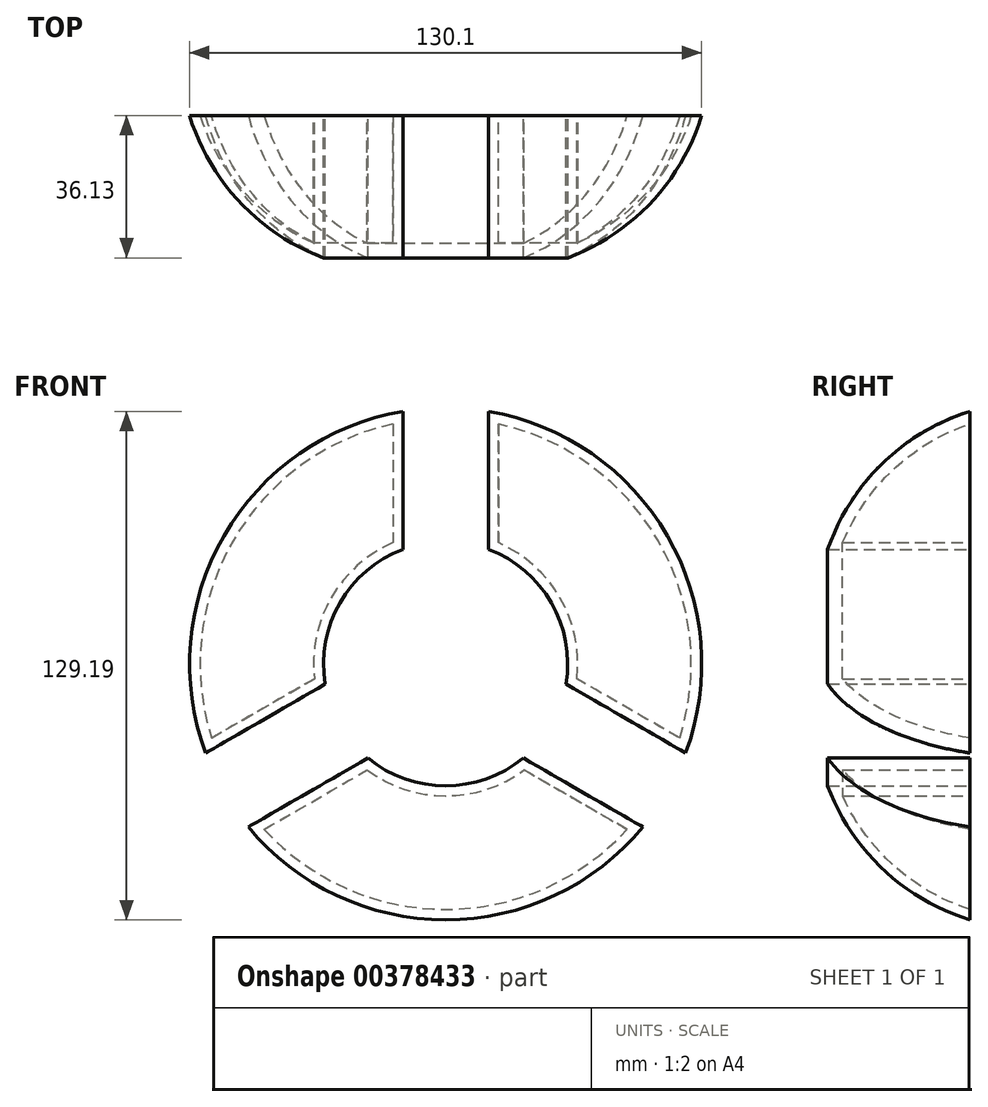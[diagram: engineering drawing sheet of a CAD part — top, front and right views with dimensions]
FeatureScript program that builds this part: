
annotation { "Feature Type Name" : "Feature", "Feature Type Description" : "" }
export const myFeature = defineFeature(function(context is Context, id is Id, definition is map)
    precondition{}
    {
        {
            var Q0;
            Q0=qCreatedBy(makeId("Front.planeOp"),FACE);
            var sketch = newSketch(context, id + "F0", { "sketchPlane" : qUnion([Q0])});
            skCircle(sketch, "E0", {"center": v(0, 0) * mm, "radius": 67.53 * mm});
            skCircle(sketch, "E1", {"center": v(0, 0) * mm, "radius": 31.02 * mm});
            skLineSegment(sketch, "E2", {"start": v(0, 31.02) * mm, "end": v(0, 67.53) * mm});
            skLineSegment(sketch, "E3.1.0", {"start": v(-26.87, -15.51) * mm, "end": v(-58.48, -33.76) * mm});
            skLineSegment(sketch, "E3.2.0", {"start": v(26.87, -15.51) * mm, "end": v(58.48, -33.76) * mm});
            skLineSegment(sketch, "E4", {"start": v(10.85, 66.65) * mm, "end": v(10.85, 29.06) * mm});
            skLineSegment(sketch, "E5.MirrorCS", {"start": v(-10.85, 66.65) * mm, "end": v(-10.85, 29.06) * mm});
            skLineSegment(sketch, "E6.1.0", {"start": v(-52.3, -42.72) * mm, "end": v(-19.74, -23.93) * mm});
            skLineSegment(sketch, "E6.1.1", {"start": v(-63.15, -23.93) * mm, "end": v(-30.6, -5.13) * mm});
            skLineSegment(sketch, "E6.2.0", {"start": v(63.15, -23.93) * mm, "end": v(30.6, -5.13) * mm});
            skLineSegment(sketch, "E6.2.1", {"start": v(52.3, -42.72) * mm, "end": v(19.74, -23.93) * mm});
            skSolve(sketch);
        }
        {
            var Q0;
            {var subQ0=sQuery(id+"F0.wireOp",EDGE,"E5.MirrorCS");Q0=makeQuery(id+"F0.imprint","IMPRINT",FACE,{"disambiguationData":[TD([[makeQuery(id+"F0.imprint","IMPRINT",EDGE,{"derivedFrom":subQ0}),-1.0]])]});}
            var Q1;
            {var subQ0=sQuery(id+"F0.wireOp",EDGE,"E4");Q1=makeQuery(id+"F0.imprint","IMPRINT",FACE,{"disambiguationData":[TD([[makeQuery(id+"F0.imprint","IMPRINT",EDGE,{"derivedFrom":subQ0}),1.0]])]});}
            var Q2;
            {var subQ0=sQuery(id+"F0.wireOp",EDGE,"E6.1.0");Q2=makeQuery(id+"F0.imprint","IMPRINT",FACE,{"disambiguationData":[TD([[makeQuery(id+"F0.imprint","IMPRINT",EDGE,{"derivedFrom":subQ0}),-1.0]])]});}
            extrude(context, id + "F1", {"entities" : qUnion([Q0, Q1, Q2]), "depth" : 36.13 * mm});
        }
        {
            var Q0;
            {var subQ0=sQuery(id+"F0.wireOp",EDGE,"E0");Q0=makeQuery(id+"F1.opExtrude","CAP_EDGE",EDGE,{"disambiguationData":[OSD([subQ0]),TDD([makeQuery(id+"F0.imprint","IMPRINT",EDGE,{"disambiguationData":[TD([[makeQuery(id+"F0.imprint","INTERSECT",VERTEX,{"derivedFrom":[subQ0,sQuery(id+"F0.wireOp",EDGE,"E4")]}),1.0]])],"derivedFrom":subQ0})])],"isStart":false});}
            var Q1;
            {var subQ0=sQuery(id+"F0.wireOp",EDGE,"E0");Q1=makeQuery(id+"F1.opExtrude","CAP_EDGE",EDGE,{"disambiguationData":[OSD([subQ0]),TDD([makeQuery(id+"F0.imprint","IMPRINT",EDGE,{"disambiguationData":[TD([[makeQuery(id+"F0.imprint","INTERSECT",VERTEX,{"derivedFrom":[subQ0,sQuery(id+"F0.wireOp",EDGE,"E5.MirrorCS")]}),-1.0]])],"derivedFrom":subQ0})])],"isStart":false});}
            var Q2;
            {var subQ0=sQuery(id+"F0.wireOp",EDGE,"E0");Q2=makeQuery(id+"F1.opExtrude","CAP_EDGE",EDGE,{"disambiguationData":[OSD([subQ0]),TDD([makeQuery(id+"F0.imprint","IMPRINT",EDGE,{"disambiguationData":[TD([[makeQuery(id+"F0.imprint","INTERSECT",VERTEX,{"derivedFrom":[subQ0,sQuery(id+"F0.wireOp",EDGE,"E6.1.0")]}),-1.0]])],"derivedFrom":subQ0})])],"isStart":false});}
            fillet(context, id + "F2", {"entities" : qUnion([Q0, Q1, Q2]), "radius" : 56.18 * mm, "tangentPropagation" : true, "allowEdgeOverflow" : false});
        }
        {
            var Q0;
            Q0=makeQuery(id+"F1.opExtrude","CAP_FACE",FACE,{"disambiguationData":[OSD([sQuery(id+"F0.wireOp",EDGE,"E0"),sQuery(id+"F0.wireOp",EDGE,"E1"),sQuery(id+"F0.wireOp",EDGE,"E5.MirrorCS"),sQuery(id+"F0.wireOp",EDGE,"E6.1.1")])],"isStart":true});
            var Q1;
            Q1=makeQuery(id+"F1.opExtrude","CAP_FACE",FACE,{"disambiguationData":[OSD([sQuery(id+"F0.wireOp",EDGE,"E0"),sQuery(id+"F0.wireOp",EDGE,"E1"),sQuery(id+"F0.wireOp",EDGE,"E6.1.0"),sQuery(id+"F0.wireOp",EDGE,"E6.2.1")])],"isStart":true});
            var Q2;
            Q2=makeQuery(id+"F1.opExtrude","CAP_FACE",FACE,{"disambiguationData":[OSD([sQuery(id+"F0.wireOp",EDGE,"E0"),sQuery(id+"F0.wireOp",EDGE,"E1"),sQuery(id+"F0.wireOp",EDGE,"E4"),sQuery(id+"F0.wireOp",EDGE,"E6.2.0")])],"isStart":true});
            shell(context, id + "F3", {"entities" : qUnion([Q0, Q1, Q2]), "thickness" : 2.54 * mm});
        }
    });
